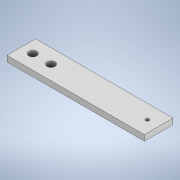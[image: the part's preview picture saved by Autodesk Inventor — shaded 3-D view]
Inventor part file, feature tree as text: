
AUTODESK INVENTOR PART (.ipt)
format: ipt  version: 2022 (Build 260153000, 153)  size: 107,520 bytes
history: native  units: in
note: dims shown in document units (in); Inventor stores cm internally (conversion verified against a paired STEP export)
features: extrude x3, sketch x3
ambient origin geometry x8: Origin, YZ Plane, XZ Plane, XY Plane, X Axis, Y Axis, Z Axis, Center Point
bodies: Solid1 (feature_tree)
feature tree (6):
  extrude  "Extrusion1"  Depth=0.9843in
  extrude  "Extrusion2"  Depth=0.1969in
  extrude  "Extrusion3"  Depth=0.7874in TaperAngle=0.0deg
  sketch  "Sketch1"  dims[d0=4.7244in d1=0.9843in]
  sketch  "Sketch2"  dims[d2=0.1969in d3=0.0in d4=0.2756in]
  sketch  "Sketch3"  dims[d5=0.2756in d6=0.7874in d7=0.0in d8=0.1181in d9=0.7874in d10=0.0in]
